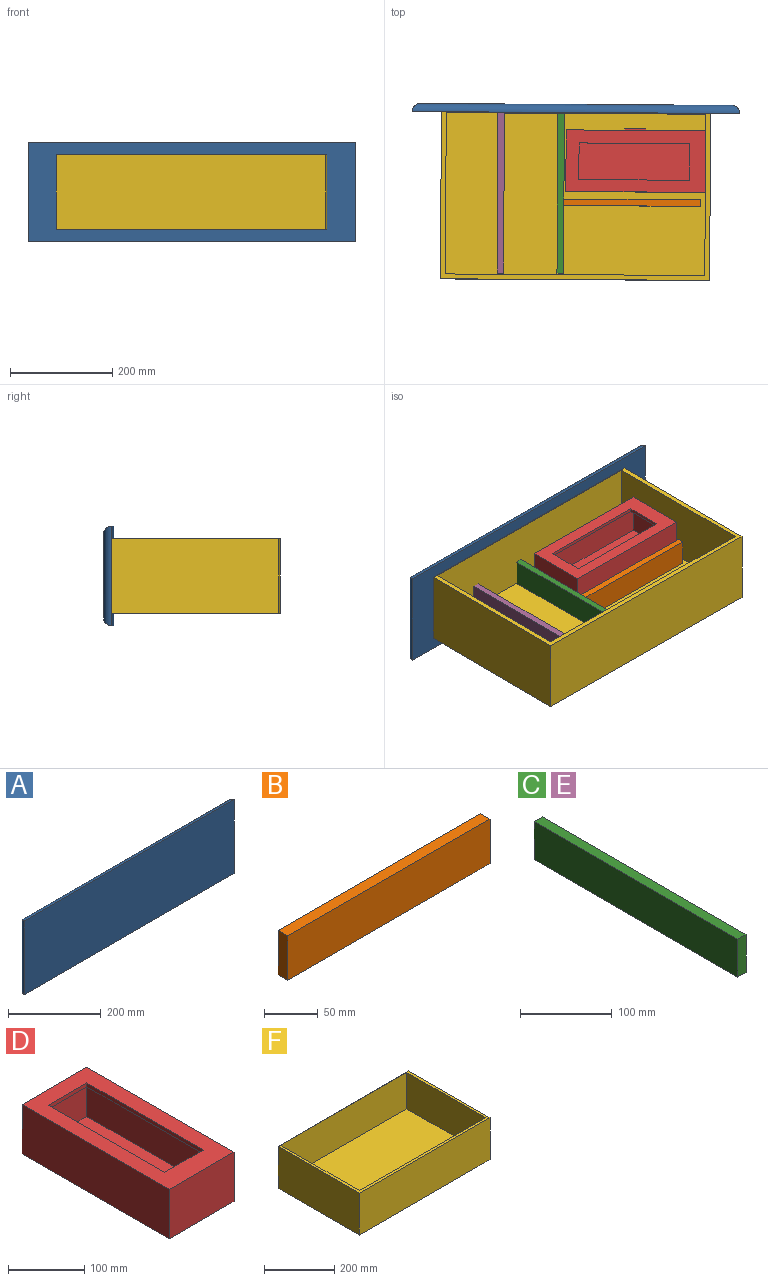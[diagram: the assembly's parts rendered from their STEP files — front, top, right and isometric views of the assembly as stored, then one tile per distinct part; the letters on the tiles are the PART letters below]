
ASSEMBLY  parts=6 mates=11
PART A: 6 faces, bbox 641.4x15.9x195.3 mm
  f0: plane 641.35x195.26mm, normal (0,-1,0), area 125231.6mm2, adj f2,f3,f4,f5
  f1: plane 609.6x163.51mm, normal (0,1,0), area 99677.2mm2, adj f2,f3,f4,f5
  f2: cylinder r=15.88mm len=195.26mm, axis (0,0,1), area 4581.4mm2, adj f0,f1,f3,f4
  f3: cylinder r=15.88mm len=641.35mm, axis (-1,0,0), area 15705.3mm2, adj f0,f1,f2,f5
  f4: cylinder r=15.88mm len=641.35mm, axis (1,0,0), area 15705.3mm2, adj f0,f1,f2,f5
  f5: cylinder r=15.88mm len=195.26mm, axis (0,0,-1), area 4581.4mm2, adj f0,f1,f3,f4
PART B: 6 faces, bbox 266.7x12.7x50.8 mm
  f0: plane 266.7x50.8mm, normal (0,1,0), area 13548.4mm2, adj f1,f3,f4,f5
  f1: plane 50.8x12.7mm, normal (-1,0,0), area 645.2mm2, adj f0,f2,f4,f5
  f2: plane 266.7x50.8mm, normal (0,-1,0), area 13548.4mm2, adj f1,f3,f4,f5
  f3: plane 50.8x12.7mm, normal (1,0,0), area 645.2mm2, adj f0,f2,f4,f5
  f4: plane 266.7x12.7mm, normal (0,0,1), area 3387.1mm2, adj f0,f1,f2,f3
  f5: plane 266.7x12.7mm, normal (0,0,-1), area 3387.1mm2, adj f0,f1,f2,f3
PART C: 6 faces, bbox 12.7x315x50.8 mm
  f0: plane 314.96x50.8mm, normal (1,0,0), area 16000mm2, adj f1,f3,f4,f5
  f1: plane 50.8x12.7mm, normal (0,1,0), area 645.2mm2, adj f0,f2,f4,f5
  f2: plane 314.96x50.8mm, normal (-1,0,0), area 16000mm2, adj f1,f3,f4,f5
  f3: plane 50.8x12.7mm, normal (0,-1,0), area 645.2mm2, adj f0,f2,f4,f5
  f4: plane 314.96x12.7mm, normal (0,0,1), area 4000mm2, adj f0,f1,f2,f3
  f5: plane 314.96x12.7mm, normal (0,0,-1), area 4000mm2, adj f0,f1,f2,f3
PART D: 21 faces, bbox 123.8x273.1x79.4 mm
  f0: plane 273.05x79.38mm, normal (1,0,0), area 21476.8mm2, adj f1,f2,f4,f5,f16,f17,f18,f19
  f1: plane 273.05x120.65mm, normal (0,0,1), area 17451.6mm2, adj f0,f2,f3,f4,f6,f7,f8,f9
  f2: plane 120.65x79.38mm, normal (0,1,0), area 9576.6mm2, adj f0,f1,f3,f5
  f3: plane 273.05x79.38mm, normal (-1,0,0), area 21673.3mm2, adj f1,f2,f4,f5
  f4: plane 120.65x79.38mm, normal (0,-1,0), area 9576.6mm2, adj f0,f1,f3,f5
  f5: plane 273.05x120.65mm, normal (0,0,-1), area 32943.5mm2, adj f0,f2,f3,f4
  f6: plane 71.76x6.35mm, normal (0,-1,0), area 455.6mm2, adj f1,f7,f9,f10
  f7: plane 215.9x6.35mm, normal (1,0,0), area 1371mm2, adj f1,f6,f8,f10
  f8: plane 71.76x6.35mm, normal (0,1,0), area 455.6mm2, adj f1,f7,f9,f10
  f9: plane 215.9x6.35mm, normal (-1,0,0), area 1371mm2, adj f1,f6,f8,f10
  f10: plane 260.35x107.95mm, normal (0,0,-1), area 12612.9mm2, adj f6,f7,f8,f9,f11,f12,f13,f14
  f11: plane 107.95x66.68mm, normal (0,-1,0), area 7197.6mm2, adj f10,f12,f14,f15
  f12: plane 260.35x66.68mm, normal (1,0,0), area 17358.8mm2, adj f10,f11,f13,f15
  f13: plane 107.95x66.68mm, normal (0,1,0), area 7197.6mm2, adj f10,f12,f14,f15
  f14: plane 260.35x66.68mm, normal (-1,0,0), area 17358.8mm2, adj f10,f11,f13,f15
  f15: plane 260.35x107.95mm, normal (0,0,1), area 28104.8mm2, adj f11,f12,f13,f14
  f16: plane 41.28x3.18mm, normal (0,0,-1), area 131mm2, adj f0,f17,f19,f20
  f17: plane 4.76x3.18mm, normal (0,1,0), area 15.1mm2, adj f0,f16,f18,f20
  f18: plane 41.28x3.18mm, normal (0,0,1), area 131mm2, adj f0,f17,f19,f20
  f19: plane 4.76x3.18mm, normal (0,-1,0), area 15.1mm2, adj f0,f16,f18,f20
  f20: plane 41.28x4.76mm, normal (1,0,0), area 196.6mm2, adj f16,f17,f18,f19
PART E: same geometry as C
PART F: 11 faces, bbox 527.1x327x146.1 mm
  f0: plane 527.05x327.03mm, normal (0,0,1), area 11875mm2, adj f1,f2,f3,f4,f6,f7,f8,f9
  f1: plane 327.03x146.05mm, normal (1,0,0), area 47762mm2, adj f0,f2,f4,f5
  f2: plane 527.05x146.05mm, normal (0,1,0), area 76975.7mm2, adj f0,f1,f3,f5
  f3: plane 327.03x146.05mm, normal (-1,0,0), area 47762mm2, adj f0,f2,f4,f5
  f4: plane 527.05x146.05mm, normal (0,-1,0), area 76975.7mm2, adj f0,f1,f3,f5
  f5: plane 527.05x327.03mm, normal (0,0,-1), area 172358.5mm2, adj f1,f2,f3,f4
  f6: plane 508x127mm, normal (0,1,0), area 64516mm2, adj f0,f7,f9,f10
  f7: plane 315.91x127mm, normal (-1,0,0), area 40120.9mm2, adj f0,f6,f8,f10
  f8: plane 508x127mm, normal (0,-1,0), area 64516mm2, adj f0,f7,f9,f10
  f9: plane 315.91x127mm, normal (1,0,0), area 40120.9mm2, adj f0,f6,f8,f10
  f10: plane 508x315.91mm, normal (0,0,1), area 160483.6mm2, adj f6,f7,f8,f9
PLACE A rot(axis=(0,0,-1),0.3deg) t=(-452.11,53,136.71)mm
PLACE B rot(axis=(0,0,-1),0.3deg) t=(-544.56,-86.73,82.74)mm
PLACE C rot(axis=(0,0,-1),0.3deg) t=(-358,-121.39,82.74)mm
PLACE D rot(axis=(0,0,1),89.7deg) t=(-335.41,-77.52,82.74)mm
PLACE E rot(axis=(0,0,-1),0.3deg) t=(-475.34,-120.7,82.74)mm
PLACE F rot(axis=(0,0,-1),0.3deg) t=(-453.17,-126.38,63.69)mm
MATE planar C.f5 <-> F.f10  axis (0,0,-1) through (-488.54,-120.14,82.74)mm
MATE planar B.f1 <-> C.f0  axis (-1,0.01,0) through (-475.94,-138.41,108.14)mm
MATE planar E.f5 <-> F.f10  axis (0,0,-1) through (-599.53,-119.49,82.74)mm
MATE parallel A.f0 <-> F.f2  axis (-0.01,-1,0) through (-452.21,37.13,136.71)mm
MATE fastened A.f0 <-> F.f2  axis (-0.01,-1,0) through (-452.21,37.13,136.71)mm
MATE planar B.f5 <-> C.f5  axis (0,0,-1) through (-342.6,-139.19,82.74)mm
MATE planar E.f1 <-> A.f0  axis (0.01,1,0) through (-598.6,37.99,108.14)mm
MATE planar F.f10 <-> D.f5  axis (0,0,1) through (-453.15,-122.41,82.74)mm
MATE planar A.f0 <-> C.f1  axis (-0.01,-1,0) through (-452.21,37.13,136.71)mm
MATE planar F.f7 <-> D.f4  axis (-1,0.01,0) through (-199.15,-123.91,146.24)mm
MATE planar A.f0 <-> C.f1  axis (-0.01,-1,0) through (-452.21,37.13,136.71)mm
